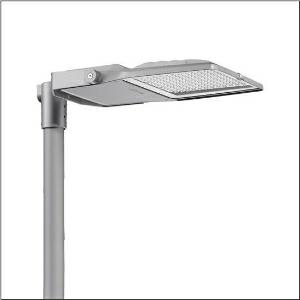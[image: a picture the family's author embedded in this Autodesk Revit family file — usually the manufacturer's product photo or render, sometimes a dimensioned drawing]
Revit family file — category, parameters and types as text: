
# Revit family: floodlight_fl_21_iq_midi___pl33t_5xa7781e2f3a_de32
name_source: partatom
category: Lighting Fixtures
units: mm (PartAtom-declared; Revit-internal decimal feet)

## family parameters
Cut with Voids When Loaded = No
Host = Face
Light Source = No
Part Type = Normal
Room Calculation Point = No
Round Connector Dimension = Use Diameter
Shared = No

## types (1)
- --- (1 x LED, 26540 lm, 208.1 W, 3000K)
    Apparent Load = 208 VA
    CIE Flux Codes = 26 75 99 100 100
    Color Rendering = 70
    Color Temperature = 3000K
    Default Elevation = 1800 mm
    Description = Floodlight FL 21 iQ midi, floodlight, primary light control with lens, of PMMA, primary optical cover: protective disc, of toughened safety glass, transparent, light distribution: PL33T, light emission: direct distribution, installation type: surface-mounted, LED, High Power LED, rated luminous flux: 26.540lm, luminous efficacy: 128lm/W, light colour: 730, colour temperature: 3000K, control gear: iQ Comfort/DALI, control: optimised constant luminous flux control (CLO 2.0), Desk-Remote (wireless, voltage-free reading and setting of iQ features in the workshop via application-optimized NFC function/RFID function), Light-Fading, Smart-Wire, Night-Set, Lumen-Switch, Temp-Guard, Auto-Match, with terminal, 6-pole, mains connection: 220..240V, AC, 50/60Hz, start of lifetime: 208W, end of service life: 227W, reduction: 90W, luminaire housing, of diecast aluminium, powder-coated, Siteco® metallic grey (DB 702S), corrosivity category C5 mid according to DIN EN ISO 12944, suitable for swimming pools, chlorine-resistant, sealing non-destructively replaceable, please order mast flange separately, mast bracket, of steel, galvanised, powder-coated, Siteco® metallic grey (DB 702S), protection rating (complete): IP66, insulation class (complete): insulation class II (safety insulation), certification: CE, ENEC, VDE, protection symbol: D, impact resistance: IK08, permissible operating ambient temperature: -40..+40°C, permissible operating ambient temperature for outdoor applications: -40..+50°C, standard: DIN EN 12944, LABS conformity tested according to VDMA 24364:2018-05, packaging unit: 1 piece

Light Distribution: PL33T
    Height = 76 mm
    Lamp = 1 x LED
    Lamp Light Flux = 26540 lm
    Lamp Power = 208.1 W
    Lamp count = 1
    Length = 657 mm
    Luminous efficacy = 128 lm/W
    Manufacturer = Siteco
    ModVariant = No
    Model = 5XA7781E2F3A
    Number of Poles = 1
    OnlyDefault = Yes
    Power Factor = 1
    Product Name = Floodlight FL 21 iQ midi | PL33T
    Product group = floodlight | pylon annexe
    ProductGroupID = 6201
    Protection Class = Protection class II
    Protection Degree = IP 66
    RLX_Detail_Level = 1
    RLX_Emergency_Light_Flux = 0 lm
    RLX_Emergency_Type = 0
    RLX_Emergency_Type_DB = No
    RlxData = <blob elided: 153857 chars, md5=9cc86ba4>
    Socket = socket
    Standby Power = 0 W
    System Light Flux = 26540 lm
    System Power = 208 W
    Type Comments = factory setting: luminous flux: 100 % | dim-lin: 254 | 710 mA
    Type Image = l_1007123.jpg
    URL = http://relux.com
    VarID = @adj_125453
    Voltage = 0 V
    Weight = 0.00 kg
    Width = 442 mm

## geometry (parser evidence)
native form markers: Blend x4, Sweep x12
no freeform markers — native parametric forms only
